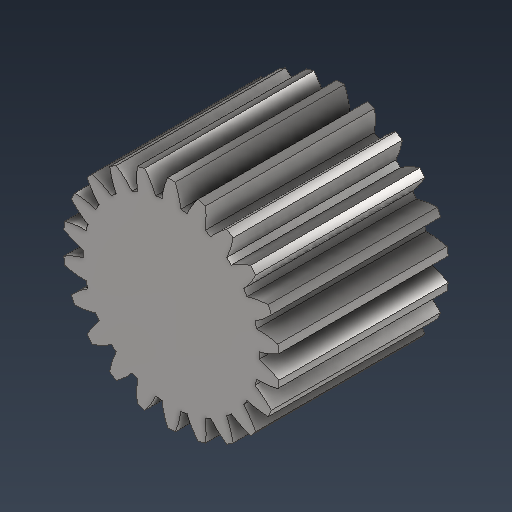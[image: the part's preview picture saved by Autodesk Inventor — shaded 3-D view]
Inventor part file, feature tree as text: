
AUTODESK INVENTOR PART (.ipt)
format: ipt  version: 2021 (Build 250183000, 183)  size: 305,152 bytes
history: native  units: mm (DEFAULTED — no unit token found)
features: plane x3, other x3, sketch x2, extrude x1
ambient origin geometry x8: Origin, YZ Plane, XZ Plane, XY Plane, X Axis, Y Axis, Z Axis, Center Point
bodies: Solid1 (feature_tree)
feature tree (9):
  extrude  "Extrusion1"  Depth=1.5mm TaperAngle=0.0deg
  plane  "Work Plane2"
  plane  "Work Plane8"
  plane  "Work Plane9"
  other  "Engrenagem reta"
  sketch  "Sketch1"  dims[d0=1.918183mm d1=1.5mm d2=0.0mm]
  sketch  "Sketch2"  dims[d3=1.76mm d4=10.0mm d5=0.0mm d16=3.188mm d17=0.0mm d34=1.427997mm d39=0.0mm d41=0.0mm d43=3.188mm d46=3.188mm d47=0.0mm d48=0.0mm]
  other  "Srf1"
  other  "Diâmetro do flanco"
